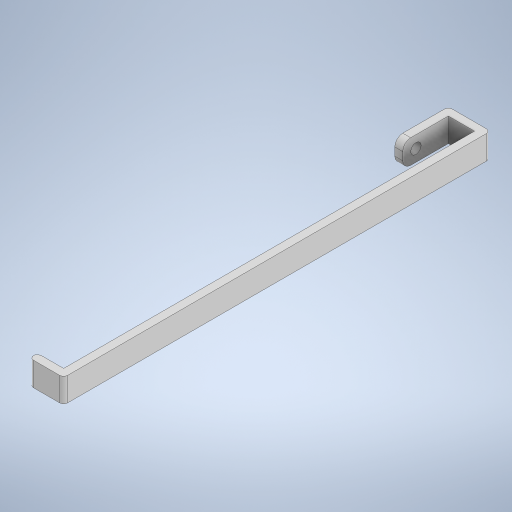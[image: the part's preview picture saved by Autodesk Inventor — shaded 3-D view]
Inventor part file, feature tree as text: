
AUTODESK INVENTOR PART (.ipt)
format: ipt  version: 2024 (Build 280153000, 153)  size: 275,456 bytes
history: native  units: in
note: dims shown in document units (in); Inventor stores cm internally (conversion verified against a paired STEP export)
features: extrude x2, fillet x2, sketch x2, projected_geometry x1
ambient origin geometry x8: Origin, YZ Plane, XZ Plane, XY Plane, X Axis, Y Axis, Z Axis, Center Point
bodies: Solid1 (feature_tree)
feature tree (7):
  extrude  "Extrusion1"  Depth=0.2598in
  extrude  "Extrusion2"  Depth=0.0787in
  fillet  "Fillet1"  Radius=0.0787in
  fillet  "Fillet2"  Radius=0.0787in
  sketch  "Sketch1"  dims[d0=4.0669in d1=0.2598in]
  sketch  "Sketch2"  dims[d2=0.0787in d3=0.0787in d4=0.0787in d5=0.0787in d6=0.5305in d7=0.2598in d8=0.2362in d9=0.0in d10=0.1043in d11=0.3996in d12=0.2362in d13=0.1181in d14=0.2362in d15=0.0in d16=0.0787in d17=0.0394in]
  projected_geometry  "Projected Loop1"
